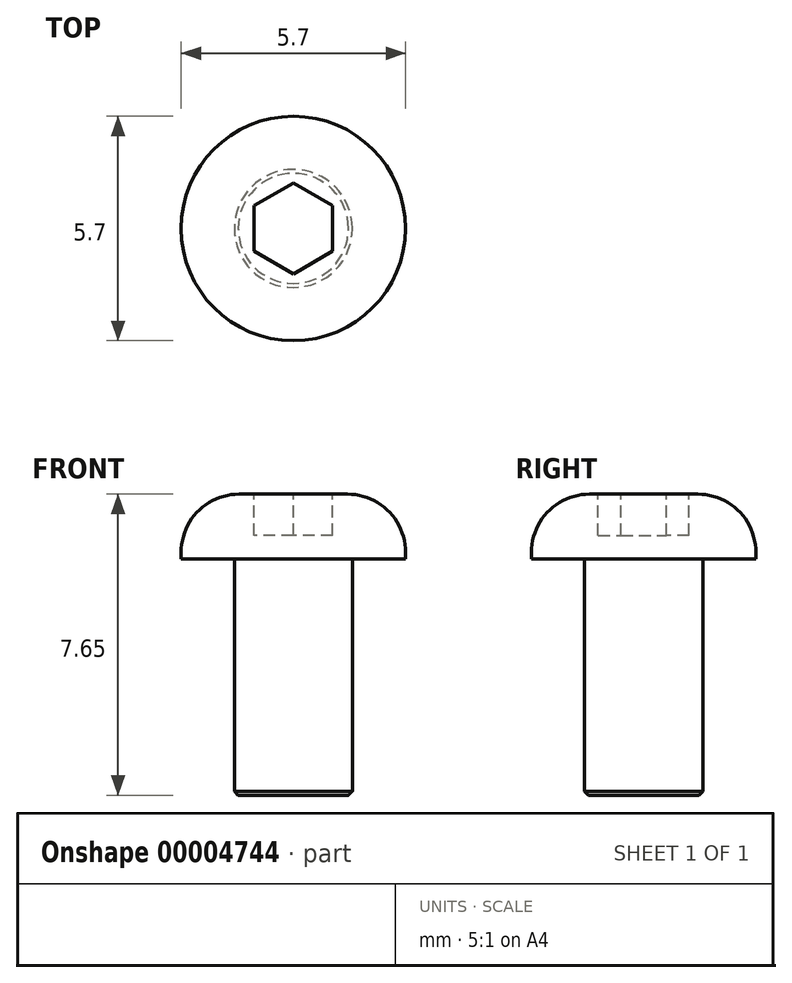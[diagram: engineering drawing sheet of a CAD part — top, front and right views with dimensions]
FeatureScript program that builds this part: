
annotation { "Feature Type Name" : "Feature", "Feature Type Description" : "" }
export const myFeature = defineFeature(function(context is Context, id is Id, definition is map)
    precondition{}
    {
        {
            var Q0;
            Q0=qCreatedBy(makeId("Top.planeOp"),FACE);
            var sketch = newSketch(context, id + "F0", { "sketchPlane" : qUnion([Q0])});
            skCircle(sketch, "E0", {"center": v(0, 0) * mm, "radius": 1.5 * mm});
            skSolve(sketch);
        }
        {
            var Q0;
            Q0 = qSketchRegion(id + "F0", true);
            extrude(context, id + "F1", {"entities" : qUnion([Q0]), "oppositeDirection" : true, "depth" : 6 * mm});
        }
        {
            var Q0;
            Q0=makeQuery(id+"F1.opExtrude","CAP_EDGE",EDGE,{"disambiguationData":[OSD([sQuery(id+"F0.wireOp",EDGE,"E0")])],"isStart":false});
            chamfer(context, id + "F2", {"entities" : qUnion([Q0]), "chamferType" : ChamferType.OFFSET_ANGLE, "width" : 0.1 * mm, "oppositeDirection" : false, "angle" : 45 * degree, "tangentPropagation" : true});
        }
        {
            var Q0;
            Q0=makeQuery(id+"F1.opExtrude","CAP_FACE",FACE,{"disambiguationData":[OSD([sQuery(id+"F0.wireOp",EDGE,"E0")])],"isStart":true});
            var sketch = newSketch(context, id + "F3", { "sketchPlane" : qUnion([Q0])});
            skCircle(sketch, "E1", {"center": v(0, 0) * mm, "radius": 2.85 * mm});
            skSolve(sketch);
        }
        {
            var Q0;
            Q0 = qSketchRegion(id + "F3", true);
            extrude(context, id + "F4", {"entities" : qUnion([Q0]), "operationType" : NewBodyOperationType.ADD, "depth" : 1.65 * mm});
        }
        {
            var Q0;
            Q0=makeQuery(id+"F4.opExtrude","CAP_FACE",FACE,{"disambiguationData":[OSD([sQuery(id+"F3.wireOp",EDGE,"E1")])],"isStart":false});
            var sketch = newSketch(context, id + "F5", { "sketchPlane" : qUnion([Q0])});
            skCircle(sketch, "E2.cCircle", {"center": v(0, 0) * mm, "radius": 1 * mm, "construction": true});
            skLineSegment(sketch, "E2.0", {"start": v(-1, -0.58) * mm, "end": v(-1, 0.58) * mm});
            skLineSegment(sketch, "E2.1", {"start": v(-1, 0.58) * mm, "end": v(0, 1.15) * mm});
            skLineSegment(sketch, "E2.2", {"start": v(0, 1.15) * mm, "end": v(1, 0.58) * mm});
            skLineSegment(sketch, "E2.3", {"start": v(1, 0.58) * mm, "end": v(1, -0.58) * mm});
            skLineSegment(sketch, "E2.4", {"start": v(1, -0.58) * mm, "end": v(0, -1.15) * mm});
            skLineSegment(sketch, "E2.5", {"start": v(0, -1.15) * mm, "end": v(-1, -0.58) * mm});
            skPoint(sketch, "E2.0.midPoint", {"position": v(-1, 0) * mm});
            skSolve(sketch);
        }
        {
            var Q0;
            Q0 = qSketchRegion(id + "F5", true);
            extrude(context, id + "F6", {"entities" : qUnion([Q0]), "operationType" : NewBodyOperationType.REMOVE, "oppositeDirection" : true, "depth" : 1.05 * mm});
        }
        {
            var Q0;
            Q0=makeQuery(id+"F4.opExtrude","CAP_EDGE",EDGE,{"disambiguationData":[OSD([sQuery(id+"F3.wireOp",EDGE,"E1")])],"isStart":false});
            fillet(context, id + "F7", {"entities" : qUnion([Q0]), "radius" : (2.95 / 2) * mm, "tangentPropagation" : true, "allowEdgeOverflow" : false});
        }
    });
